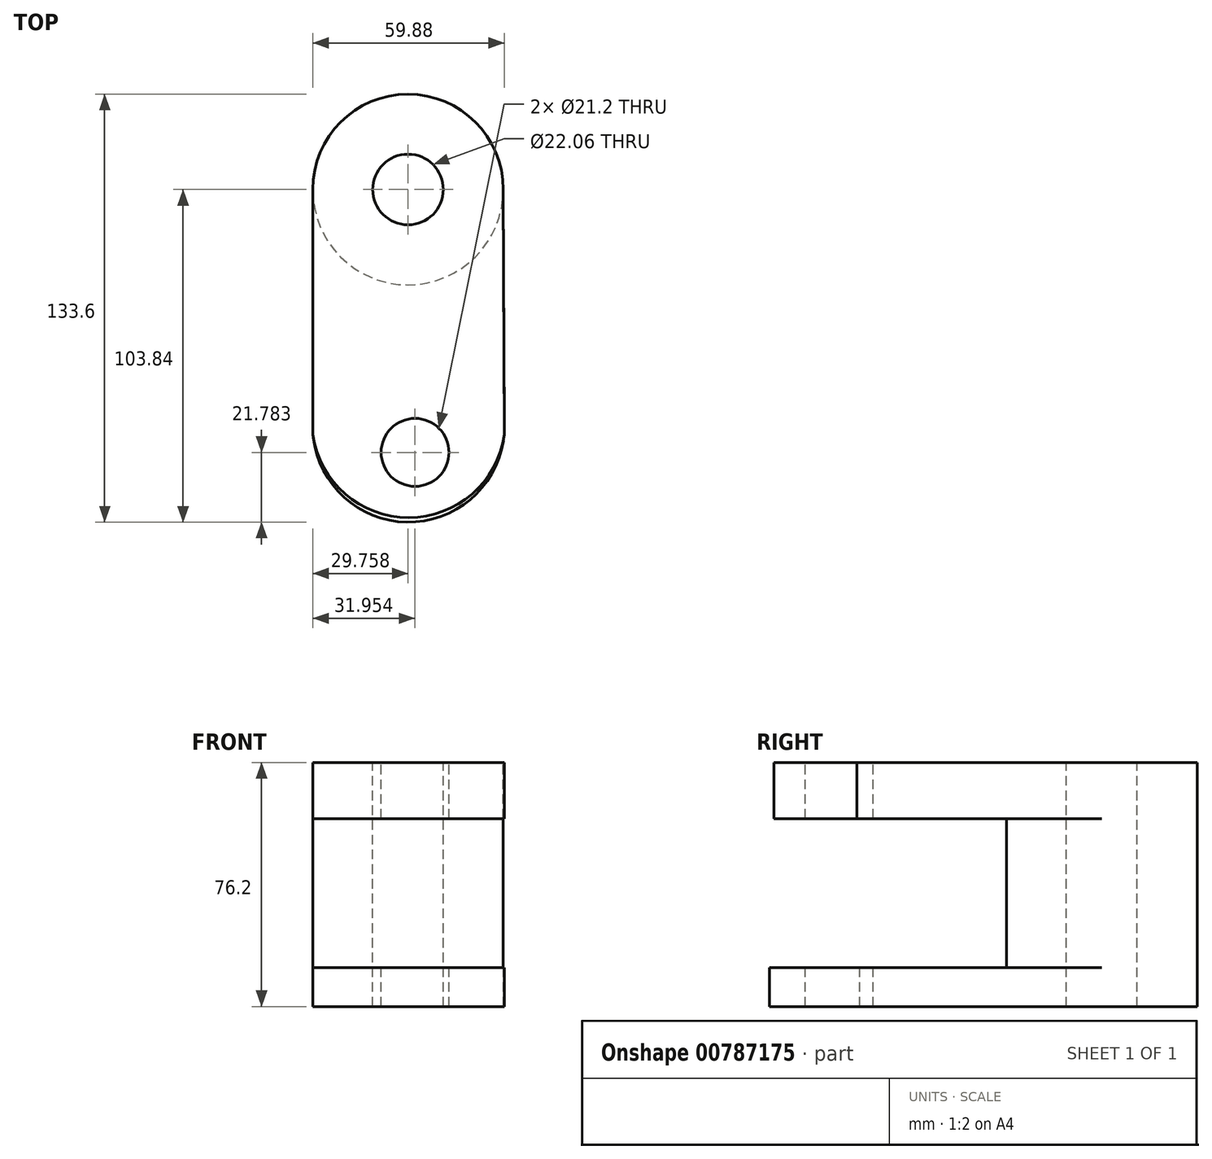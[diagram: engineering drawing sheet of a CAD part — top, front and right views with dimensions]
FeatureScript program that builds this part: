
annotation { "Feature Type Name" : "Feature", "Feature Type Description" : "" }
export const myFeature = defineFeature(function(context is Context, id is Id, definition is map)
    precondition{}
    {
        {
            var Q0;
            Q0=qCreatedBy(makeId("Top.planeOp"),FACE);
            var sketch = newSketch(context, id + "F0", { "sketchPlane" : qUnion([Q0])});
            skCircle(sketch, "E0", {"center": v(-30.12, 0) * mm, "radius": 29.76 * mm});
            skSolve(sketch);
        }
        {
            var Q0;
            Q0=makeQuery(id+"F0.imprint","IMPRINT",FACE,{"disambiguationData":[TD([[makeQuery(id+"F0.imprint","IMPRINT",EDGE,{"derivedFrom":sQuery(id+"F0.wireOp",EDGE,"E0")}),1.0]])]});
            extrude(context, id + "F1", {"entities" : qUnion([Q0]), "depth" : 76.2 * mm, "offsetDistance" : 25.4 * mm});
        }
        {
            var Q0;
            Q0=makeQuery(id+"F1.opExtrude","CAP_FACE",FACE,{"disambiguationData":[OSD([sQuery(id+"F0.wireOp",EDGE,"E0")])],"isStart":false});
            var sketch = newSketch(context, id + "F2", { "sketchPlane" : qUnion([Q0])});
            skCircle(sketch, "E1", {"center": v(-30.12, 0) * mm, "radius": 11.03 * mm});
            skSolve(sketch);
        }
        {
            var Q0;
            Q0=makeQuery(id+"F2.imprint","IMPRINT",FACE,{"disambiguationData":[TD([[makeQuery(id+"F2.imprint","IMPRINT",EDGE,{"derivedFrom":sQuery(id+"F2.wireOp",EDGE,"E1")}),1.0]])]});
            extrude(context, id + "F3", {"entities" : qUnion([Q0]), "operationType" : NewBodyOperationType.REMOVE, "oppositeDirection" : true, "depth" : 120.14 * mm, "offsetDistance" : 25.4 * mm});
        }
        {
            var Q0;
            Q0=makeQuery(id+"F1.opExtrude","CAP_FACE",FACE,{"disambiguationData":[OSD([sQuery(id+"F0.wireOp",EDGE,"E0")])],"isStart":true});
            var sketch = newSketch(context, id + "F4", { "sketchPlane" : qUnion([Q0])});
            skLineSegment(sketch, "E2", {"start": v(-59.88, 0) * mm, "end": v(-59.88, 75.8) * mm});
            skArc(sketch, "E3", {"start": v(0, 73.86) * mm, "mid": v(-29, 103.82) * mm, "end": v(-59.88, 75.8) * mm});
            skLineSegment(sketch, "E4", {"start": v(-0.36, 0) * mm, "end": v(0, 73.86) * mm});
            skSolve(sketch);
        }
        {
            var Q0;
            {var subQ0=sQuery(id+"F4.wireOp",EDGE,"E2");Q0=makeQuery(id+"F4.imprint","IMPRINT",FACE,{"disambiguationData":[TD([[makeQuery(id+"F4.imprint","IMPRINT",EDGE,{"derivedFrom":subQ0}),-1.0]])]});}
            extrude(context, id + "F5", {"entities" : qUnion([Q0]), "operationType" : NewBodyOperationType.ADD, "oppositeDirection" : true, "depth" : 12.2 * mm, "offsetDistance" : 25.4 * mm});
        }
        {
            var Q0;
            Q0=makeQuery(id+"F1.opExtrude","CAP_FACE",FACE,{"disambiguationData":[OSD([sQuery(id+"F0.wireOp",EDGE,"E0")])],"isStart":false});
            var sketch = newSketch(context, id + "F6", { "sketchPlane" : qUnion([Q0])});
            skLineSegment(sketch, "E5", {"start": v(-0.36, 0) * mm, "end": v(0, -76.47) * mm});
            skLineSegment(sketch, "E6", {"start": v(-59.88, 0) * mm, "end": v(-59.88, -76.47) * mm});
            skArc(sketch, "E7", {"start": v(-59.88, -76.47) * mm, "mid": v(-29.94, -102.42) * mm, "end": v(0, -76.47) * mm});
            skSolve(sketch);
        }
        {
            var Q0;
            {var subQ0=sQuery(id+"F6.wireOp",EDGE,"E5");Q0=makeQuery(id+"F6.imprint","IMPRINT",FACE,{"disambiguationData":[TD([[makeQuery(id+"F6.imprint","IMPRINT",EDGE,{"derivedFrom":subQ0}),-1.0]])]});}
            extrude(context, id + "F7", {"entities" : qUnion([Q0]), "operationType" : NewBodyOperationType.ADD, "oppositeDirection" : true, "depth" : 17.53 * mm, "offsetDistance" : 25.4 * mm});
        }
        {
            var Q0;
            {var subQ0=sQuery(id+"F0.wireOp",EDGE,"E0");Q0=makeQuery(id+"F7.boolean.opBoolean","MERGE",FACE,{"derivedFrom":[makeQuery(id+"F1.opExtrude","CAP_FACE",FACE,{"disambiguationData":[OSD([subQ0])],"isStart":false}),makeQuery(id+"F7.opExtrude","CAP_FACE",FACE,{"disambiguationData":[OSD([subQ0,sQuery(id+"F6.wireOp",EDGE,"E5"),sQuery(id+"F6.wireOp",EDGE,"E6"),sQuery(id+"F6.wireOp",EDGE,"E7")])],"isStart":true})]});}
            var sketch = newSketch(context, id + "F8", { "sketchPlane" : qUnion([Q0])});
            skCircle(sketch, "E8", {"center": v(-27.93, -82.06) * mm, "radius": 10.6 * mm});
            skSolve(sketch);
        }
        {
            var Q0;
            Q0=makeQuery(id+"F8.imprint","IMPRINT",FACE,{"disambiguationData":[TD([[makeQuery(id+"F8.imprint","IMPRINT",EDGE,{"derivedFrom":sQuery(id+"F8.wireOp",EDGE,"E8")}),1.0]])]});
            extrude(context, id + "F9", {"entities" : qUnion([Q0]), "operationType" : NewBodyOperationType.REMOVE, "oppositeDirection" : true, "depth" : 148.6 * mm, "offsetDistance" : 25.4 * mm});
        }
    });
